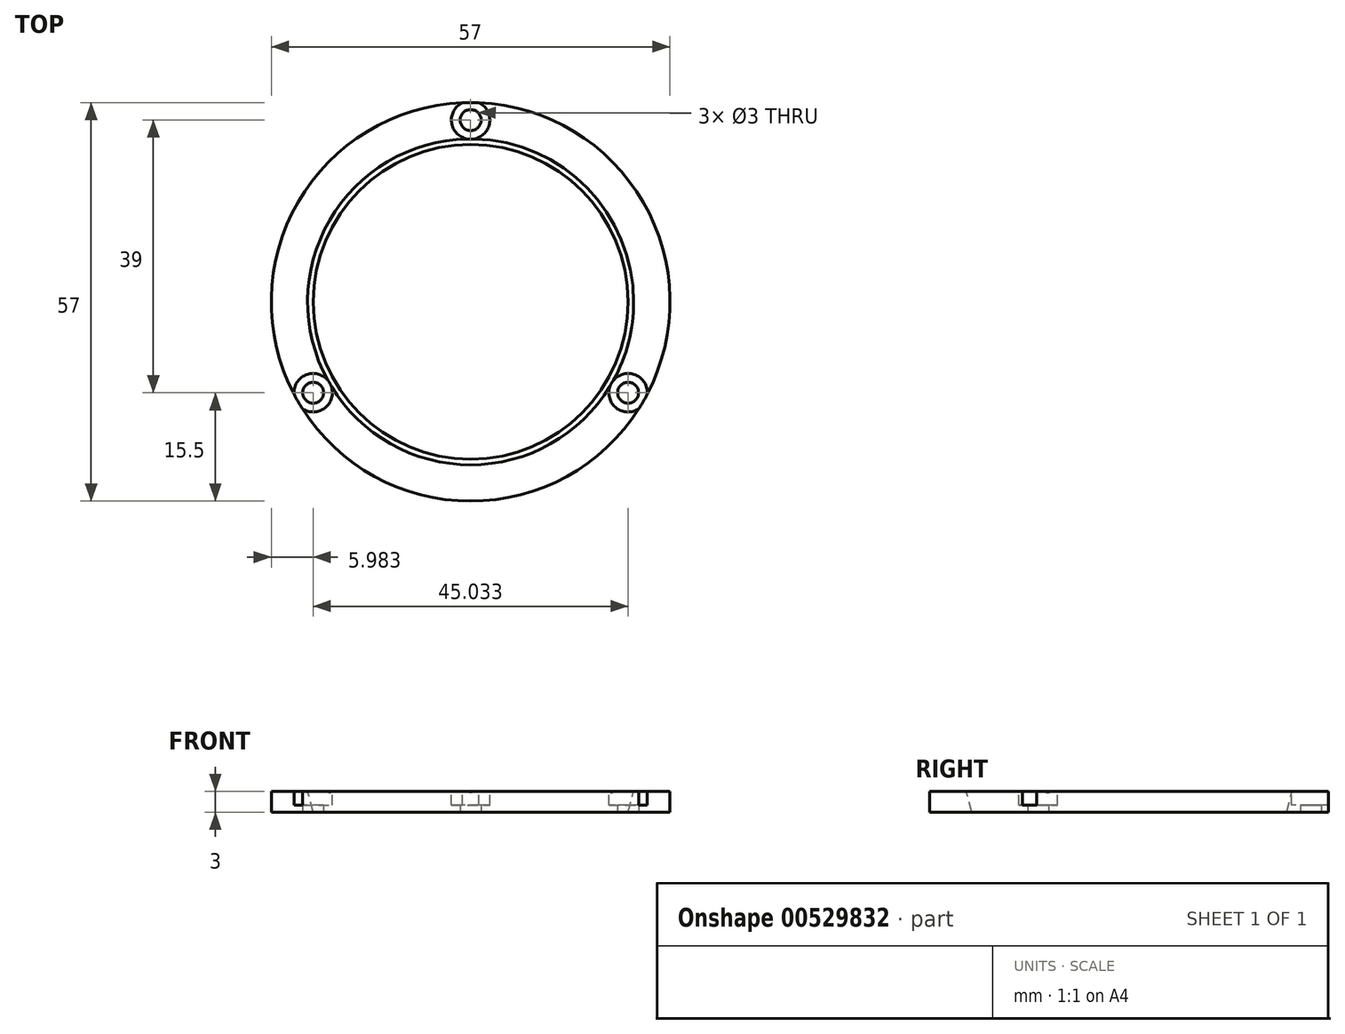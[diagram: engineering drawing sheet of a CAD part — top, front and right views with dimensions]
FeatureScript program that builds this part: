
annotation { "Feature Type Name" : "Feature", "Feature Type Description" : "" }
export const myFeature = defineFeature(function(context is Context, id is Id, definition is map)
    precondition{}
    {
        {
            var Q0;
            Q0=qCreatedBy(makeId("Top.planeOp"),FACE);
            var sketch = newSketch(context, id + "F0", { "sketchPlane" : qUnion([Q0])});
            skCircle(sketch, "E0", {"center": v(0, 0) * mm, "radius": 22.5 * mm});
            skCircle(sketch, "E1", {"center": v(0, 0) * mm, "radius": 28.5 * mm});
            skCircle(sketch, "E2", {"center": v(0, 26) * mm, "radius": 1.5 * mm});
            skLineSegment(sketch, "E3", {"start": v(0, 0) * mm, "end": v(-22.52, -13) * mm, "construction": true});
            skLineSegment(sketch, "E4", {"start": v(0, 0) * mm, "end": v(22.52, -13) * mm, "construction": true});
            skCircle(sketch, "E5", {"center": v(-22.52, -13) * mm, "radius": 1.5 * mm});
            skCircle(sketch, "E6", {"center": v(22.52, -13) * mm, "radius": 1.5 * mm});
            skSolve(sketch);
        }
        {
            var Q0;
            Q0=makeQuery(id+"F0.imprint","IMPRINT",FACE,{"disambiguationData":[TD([[makeQuery(id+"F0.imprint","IMPRINT",EDGE,{"derivedFrom":sQuery(id+"F0.wireOp",EDGE,"E0")}),-1.0]])]});
            extrude(context, id + "F1", {"entities" : qUnion([Q0]), "depth" : 3 * mm, "offsetDistance" : 25 * mm});
        }
        {
            var Q0;
            Q0=makeQuery(id+"F1.opExtrude","CAP_FACE",FACE,{"disambiguationData":[OSD([sQuery(id+"F0.wireOp",EDGE,"E0"),sQuery(id+"F0.wireOp",EDGE,"E1"),sQuery(id+"F0.wireOp",EDGE,"E2"),sQuery(id+"F0.wireOp",EDGE,"E5"),sQuery(id+"F0.wireOp",EDGE,"E6")])],"isStart":false});
            var sketch = newSketch(context, id + "F2", { "sketchPlane" : qUnion([Q0])});
            skCircle(sketch, "E7", {"center": v(0, 26) * mm, "radius": 2.75 * mm});
            skCircle(sketch, "E8", {"center": v(-22.52, -13) * mm, "radius": 2.75 * mm});
            skCircle(sketch, "E9", {"center": v(22.52, -13) * mm, "radius": 2.75 * mm});
            skSolve(sketch);
        }
        {
            var Q0;
            {var subQ0=sQuery(id+"F0.wireOp",EDGE,"E2");Q0=makeQuery(id+"F2.imprint","IMPRINT",FACE,{"disambiguationData":[TD([[makeQuery(id+"F2.imprint","IMPRINT",EDGE,{"derivedFrom":makeQuery(id+"F1.opExtrude","CAP_EDGE",EDGE,{"disambiguationData":[OSD([subQ0])],"isStart":false})}),-1.0]])]});}
            var Q1;
            {var subQ0=sQuery(id+"F0.wireOp",EDGE,"E5");Q1=makeQuery(id+"F2.imprint","IMPRINT",FACE,{"disambiguationData":[TD([[makeQuery(id+"F2.imprint","IMPRINT",EDGE,{"derivedFrom":makeQuery(id+"F1.opExtrude","CAP_EDGE",EDGE,{"disambiguationData":[OSD([subQ0])],"isStart":false})}),-1.0]])]});}
            var Q2;
            {var subQ5=sQuery(id+"F0.wireOp",EDGE,"E6");Q2=makeQuery(id+"F2.imprint","IMPRINT",FACE,{"disambiguationData":[TD([[makeQuery(id+"F2.imprint","IMPRINT",EDGE,{"derivedFrom":makeQuery(id+"F1.opExtrude","CAP_EDGE",EDGE,{"disambiguationData":[OSD([subQ5])],"isStart":false})}),-1.0]])]});}
            extrude(context, id + "F3", {"entities" : qUnion([Q0, Q1, Q2]), "operationType" : NewBodyOperationType.REMOVE, "oppositeDirection" : true, "depth" : 2 * mm, "offsetDistance" : 25 * mm});
        }
        {
            var Q0;
            Q0=qCreatedBy(makeId("Front.planeOp"),FACE);
            var sketch = newSketch(context, id + "F4", { "sketchPlane" : qUnion([Q0])});
            skLineSegment(sketch, "E10", {"start": v(-22.5, 0) * mm, "end": v(-23.84, 5) * mm});
            skLineSegment(sketch, "E11", {"start": v(-22.5, 0) * mm, "end": v(-22.5, 5) * mm});
            skLineSegment(sketch, "E12", {"start": v(-22.5, 5) * mm, "end": v(-23.84, 5) * mm});
            skLineSegment(sketch, "E13", {"start": v(0, 0) * mm, "end": v(0, 4.4) * mm, "construction": true});
            skSolve(sketch);
        }
        {
            var Q0;
            Q0=makeQuery(id+"F4.imprint","IMPRINT",FACE,{"disambiguationData":[TD([[makeQuery(id+"F4.imprint","IMPRINT",EDGE,{"derivedFrom":sQuery(id+"F4.wireOp",EDGE,"E10")}),-1.0]])]});
            var Q1;
            Q1=sQuery(id+"F4.wireOp",EDGE,"E13");
            revolve(context, id + "F5", {"operationType" : NewBodyOperationType.REMOVE, "entities" : qUnion([Q0]), "axis" : qUnion([Q1]), "revolveType" : RevolveType.FULL, "oppositeDirection" : true});
        }
    });
